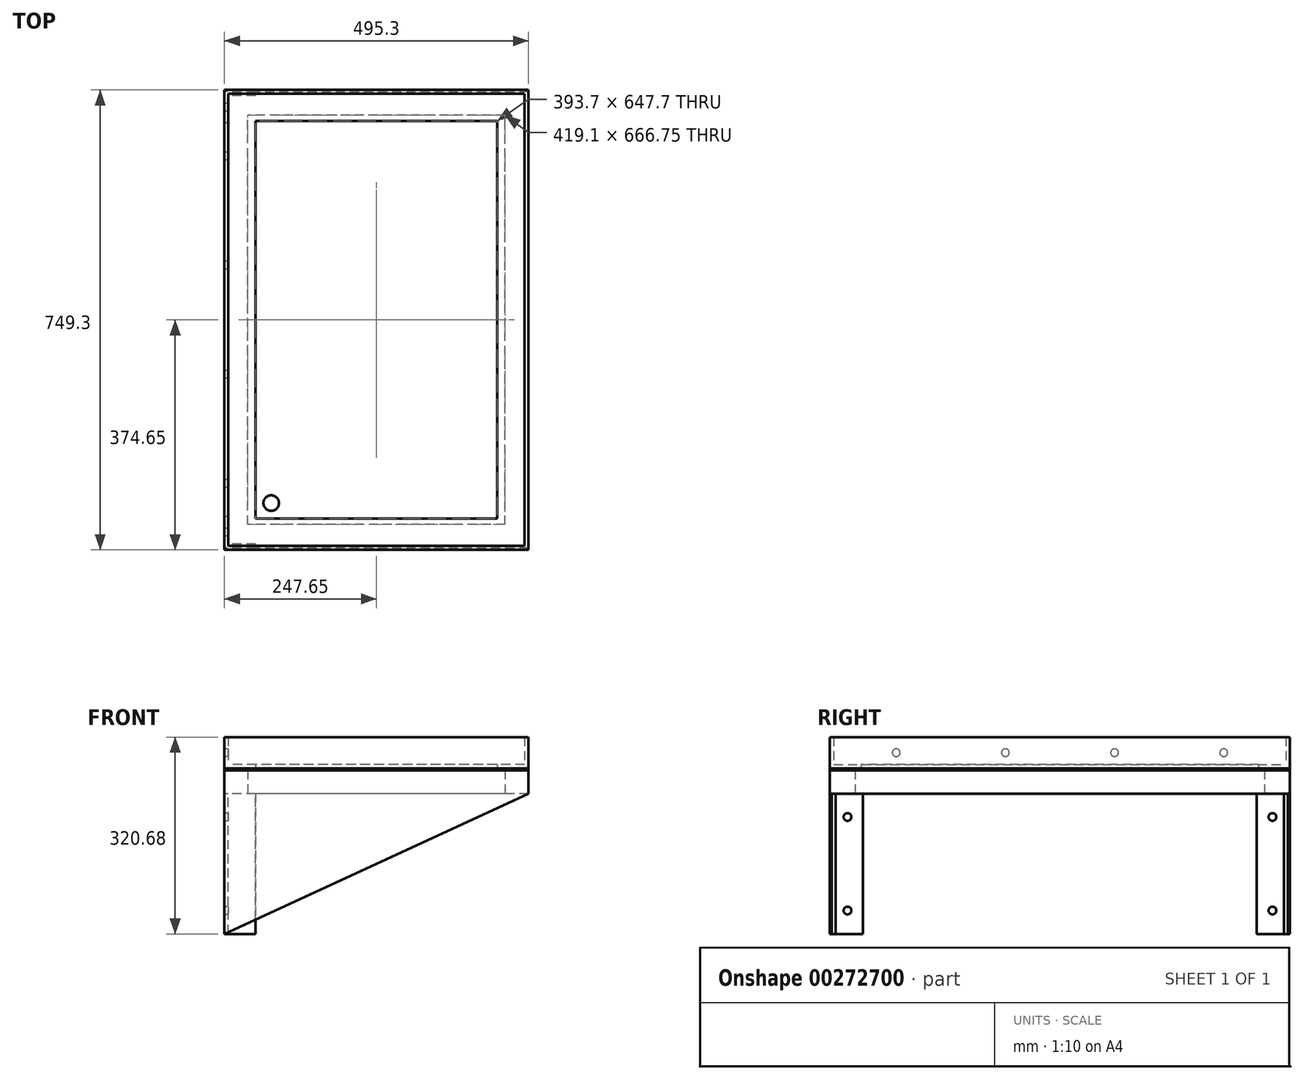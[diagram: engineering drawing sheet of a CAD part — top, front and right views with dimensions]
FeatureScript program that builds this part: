
annotation { "Feature Type Name" : "Feature", "Feature Type Description" : "" }
export const myFeature = defineFeature(function(context is Context, id is Id, definition is map)
    precondition{}
    {
        {
            var Q0;
            Q0=qCreatedBy(makeId("Top.planeOp"),FACE);
            var sketch = newSketch(context, id + "F0", { "sketchPlane" : qUnion([Q0])});
            skLineSegment(sketch, "E0.bottom", {"start": v(247.65, -371.47) * mm, "end": v(-247.65, -371.48) * mm});
            skLineSegment(sketch, "E0.top", {"start": v(247.65, 371.48) * mm, "end": v(-247.65, 371.48) * mm});
            skLineSegment(sketch, "E0.left", {"start": v(247.65, -371.47) * mm, "end": v(247.65, 371.48) * mm});
            skLineSegment(sketch, "E0.right", {"start": v(-247.65, -371.48) * mm, "end": v(-247.65, 371.48) * mm});
            skPoint(sketch, "E0.middle", {"position": v(0, 0) * mm});
            skLineSegment(sketch, "E1.0", {"start": v(-209.55, -333.38) * mm, "end": v(-209.55, 333.38) * mm});
            skLineSegment(sketch, "E1.1", {"start": v(209.55, -333.37) * mm, "end": v(-209.55, -333.38) * mm});
            skLineSegment(sketch, "E1.2", {"start": v(209.55, -333.37) * mm, "end": v(209.55, 333.38) * mm});
            skLineSegment(sketch, "E1.3", {"start": v(209.55, 333.38) * mm, "end": v(-209.55, 333.38) * mm});
            skSolve(sketch);
        }
        {
            var Q0;
            Q0 = qSketchRegion(id + "F0", true);
            extrude(context, id + "F1", {"entities" : qUnion([Q0]), "depth" : 38.1 * mm});
        }
        {
            var Q0;
            Q0=makeQuery(id+"F1.opExtrude","SWEPT_FACE",FACE,{"disambiguationData":[OSD([sQuery(id+"F0.wireOp",EDGE,"E0.bottom")])]});
            var sketch = newSketch(context, id + "F2", { "sketchPlane" : qUnion([Q0])});
            skLineSegment(sketch, "E2.0", {"start": v(247.65, 38.1) * mm, "end": v(-247.65, 38.1) * mm});
            skLineSegment(sketch, "E3", {"start": v(247.65, 0) * mm, "end": v(-247.65, -228.6) * mm});
            skLineSegment(sketch, "E4", {"start": v(-247.65, -228.6) * mm, "end": v(-247.65, 0) * mm});
            skLineSegment(sketch, "E5", {"start": v(-247.65, 0) * mm, "end": v(-247.65, 38.1) * mm});
            skLineSegment(sketch, "E6", {"start": v(247.65, 38.1) * mm, "end": v(247.65, 0) * mm});
            skSolve(sketch);
        }
        {
            var Q0;
            Q0=makeQuery(id+"F1.opExtrude","SWEPT_FACE",FACE,{"disambiguationData":[OSD([sQuery(id+"F0.wireOp",EDGE,"E0.top")])]});
            var sketch = newSketch(context, id + "F3", { "sketchPlane" : qUnion([Q0])});
            skLineSegment(sketch, "E7", {"start": v(-247.65, 0) * mm, "end": v(247.65, -228.6) * mm});
            skLineSegment(sketch, "E8", {"start": v(247.65, -228.6) * mm, "end": v(247.65, 0) * mm});
            skLineSegment(sketch, "E9", {"start": v(-247.65, 0) * mm, "end": v(-247.65, 38.1) * mm});
            skLineSegment(sketch, "E10", {"start": v(-247.65, 38.1) * mm, "end": v(247.65, 38.1) * mm});
            skLineSegment(sketch, "E11", {"start": v(247.65, 38.1) * mm, "end": v(247.65, 0) * mm});
            skSolve(sketch);
        }
        {
            var Q0;
            Q0 = qSketchRegion(id + "F2", true);
            extrude(context, id + "F4", {"entities" : qUnion([Q0]), "depth" : 3.17 * mm});
        }
        {
            var Q0;
            Q0 = qSketchRegion(id + "F3", true);
            extrude(context, id + "F5", {"entities" : qUnion([Q0]), "depth" : 3.17 * mm});
        }
        {
            var Q0;
            Q0=makeQuery(id+"F5.boolean.opBoolean","MERGE",FACE,{"derivedFrom":[makeQuery(id+"F4.boolean.opBoolean","MERGE",FACE,{"derivedFrom":[makeQuery(id+"F1.opExtrude","SWEPT_FACE",FACE,{"disambiguationData":[OSD([sQuery(id+"F0.wireOp",EDGE,"E0.right")])]}),makeQuery(id+"F4.opExtrude","SWEPT_FACE",FACE,{"disambiguationData":[OSD([sQuery(id+"F2.wireOp",EDGE,"E4")])]})]}),makeQuery(id+"F5.opExtrude","SWEPT_FACE",FACE,{"disambiguationData":[OSD([sQuery(id+"F3.wireOp",EDGE,"E8")])]})]});
            var sketch = newSketch(context, id + "F6", { "sketchPlane" : qUnion([Q0])});
            skLineSegment(sketch, "E12.0", {"start": v(371.47, 0) * mm, "end": v(-371.48, 0) * mm});
            skLineSegment(sketch, "E13", {"start": v(-320.68, -228.6) * mm, "end": v(-320.68, 0) * mm});
            skLineSegment(sketch, "E14", {"start": v(371.47, 0) * mm, "end": v(371.47, -228.6) * mm});
            skLineSegment(sketch, "E15", {"start": v(371.47, -228.6) * mm, "end": v(320.68, -228.6) * mm});
            skLineSegment(sketch, "E16", {"start": v(320.68, -228.6) * mm, "end": v(320.68, 0) * mm});
            skLineSegment(sketch, "E17", {"start": v(-320.68, -228.6) * mm, "end": v(-371.48, -228.6) * mm});
            skLineSegment(sketch, "E18", {"start": v(-371.48, 0) * mm, "end": v(-371.48, -228.6) * mm});
            skSolve(sketch);
        }
        {
            var Q0;
            Q0 = qSketchRegion(id + "F6", true);
            extrude(context, id + "F7", {"entities" : qUnion([Q0]), "oppositeDirection" : true, "depth" : 6.35 * mm});
        }
        {
            var Q0;
            Q0=makeQuery(id+"F7.opExtrude","CAP_FACE",FACE,{"disambiguationData":[OSD([sQuery(id+"F6.wireOp",EDGE,"E12.0"),sQuery(id+"F6.wireOp",EDGE,"e24fae86-0eb9-4a12-ab5b-77b361595a97.0"),sQuery(id+"F6.wireOp",EDGE,"e9ZgIQYv-HXcm-3d7P-bhbC-L1sBMD0jo2iH"),sQuery(id+"F6.wireOp",EDGE,"b7fAcNB5-LM3v-M6Ys-QrrH-VZOuPliIFRUq")])],"isStart":false});
            var sketch = newSketch(context, id + "F8", { "sketchPlane" : qUnion([Q0])});
            skLineSegment(sketch, "E19.bottom", {"start": v(-371.48, -228.6) * mm, "end": v(-365.13, -228.6) * mm});
            skLineSegment(sketch, "E19.top", {"start": v(-371.48, 0) * mm, "end": v(-365.13, 0) * mm});
            skLineSegment(sketch, "E19.left", {"start": v(-371.48, -228.6) * mm, "end": v(-371.48, 0) * mm});
            skLineSegment(sketch, "E19.right", {"start": v(-365.13, -228.6) * mm, "end": v(-365.13, 0) * mm});
            skSolve(sketch);
        }
        {
            var Q0;
            Q0 = qSketchRegion(id + "F8", true);
            extrude(context, id + "F9", {"entities" : qUnion([Q0]), "operationType" : NewBodyOperationType.ADD, "depth" : 44.45 * mm});
        }
        {
            var Q0;
            Q0=makeQuery(id+"F7.opExtrude","CAP_FACE",FACE,{"disambiguationData":[OSD([sQuery(id+"F6.wireOp",EDGE,"f5ba7e4f-57d3-4fa4-9deb-a295e54d8ec9.0"),sQuery(id+"F6.wireOp",EDGE,"E12.0"),sQuery(id+"F6.wireOp",EDGE,"EwE4f2qn-rMHZ-ifyL-MpHM-OiWTRZvf5JZf"),sQuery(id+"F6.wireOp",EDGE,"E13")])],"isStart":false});
            var sketch = newSketch(context, id + "F10", { "sketchPlane" : qUnion([Q0])});
            skLineSegment(sketch, "E20.bottom", {"start": v(371.48, -228.6) * mm, "end": v(365.13, -228.6) * mm});
            skLineSegment(sketch, "E20.top", {"start": v(371.48, 0) * mm, "end": v(365.13, 0) * mm});
            skLineSegment(sketch, "E20.left", {"start": v(371.48, -228.6) * mm, "end": v(371.48, 0) * mm});
            skLineSegment(sketch, "E20.right", {"start": v(365.13, -228.6) * mm, "end": v(365.13, 0) * mm});
            skSolve(sketch);
        }
        {
            var Q0;
            Q0 = qSketchRegion(id + "F10", true);
            extrude(context, id + "F11", {"entities" : qUnion([Q0]), "operationType" : NewBodyOperationType.ADD, "depth" : 44.45 * mm});
        }
        {
            var Q0;
            Q0=makeQuery(id+"F1.opExtrude","CAP_FACE",FACE,{"disambiguationData":[OSD([sQuery(id+"F0.wireOp",EDGE,"E0.bottom"),sQuery(id+"F0.wireOp",EDGE,"E0.top"),sQuery(id+"F0.wireOp",EDGE,"E0.left"),sQuery(id+"F0.wireOp",EDGE,"E0.right"),sQuery(id+"F0.wireOp",EDGE,"E1.0"),sQuery(id+"F0.wireOp",EDGE,"E1.1"),sQuery(id+"F0.wireOp",EDGE,"E1.2"),sQuery(id+"F0.wireOp",EDGE,"E1.3")])],"isStart":false});
            var sketch = newSketch(context, id + "F12", { "sketchPlane" : qUnion([Q0])});
            skLineSegment(sketch, "E21.0", {"start": v(247.65, 374.65) * mm, "end": v(-247.65, 374.65) * mm});
            skLineSegment(sketch, "E22.0", {"start": v(247.65, -374.65) * mm, "end": v(-247.65, -374.65) * mm});
            skLineSegment(sketch, "E23", {"start": v(-247.65, -374.65) * mm, "end": v(-247.65, 374.65) * mm});
            skLineSegment(sketch, "E24", {"start": v(247.65, 374.65) * mm, "end": v(247.65, -374.65) * mm});
            skCircle(sketch, "E25", {"center": v(-171.45, -298.45) * mm, "radius": 12.7 * mm});
            skSolve(sketch);
        }
        {
            var Q0;
            Q0 = qSketchRegion(id + "F12", true);
            extrude(context, id + "F13", {"entities" : qUnion([Q0]), "depth" : 3.17 * mm});
        }
        {
            var Q0;
            Q0=makeQuery(id+"F13.opExtrude","CAP_FACE",FACE,{"disambiguationData":[OSD([sQuery(id+"F12.wireOp",EDGE,"E21.0"),sQuery(id+"F12.wireOp",EDGE,"E22.0"),sQuery(id+"F12.wireOp",EDGE,"E23"),sQuery(id+"F12.wireOp",EDGE,"E24")])],"isStart":false});
            var sketch = newSketch(context, id + "F14", { "sketchPlane" : qUnion([Q0])});
            skLineSegment(sketch, "E26.0.0", {"start": v(247.65, -374.65) * mm, "end": v(247.65, 374.65) * mm});
            skLineSegment(sketch, "E26.0.1", {"start": v(247.65, 374.65) * mm, "end": v(-247.65, 374.65) * mm});
            skLineSegment(sketch, "E26.0.2", {"start": v(-247.65, 374.65) * mm, "end": v(-247.65, -374.65) * mm});
            skLineSegment(sketch, "E26.0.3", {"start": v(-247.65, -374.65) * mm, "end": v(247.65, -374.65) * mm});
            skLineSegment(sketch, "E27.0", {"start": v(-196.85, 323.85) * mm, "end": v(-196.85, -323.85) * mm});
            skLineSegment(sketch, "E27.1", {"start": v(196.85, 323.85) * mm, "end": v(-196.85, 323.85) * mm});
            skLineSegment(sketch, "E27.2", {"start": v(196.85, -323.85) * mm, "end": v(196.85, 323.85) * mm});
            skLineSegment(sketch, "E27.3", {"start": v(-196.85, -323.85) * mm, "end": v(196.85, -323.85) * mm});
            skSolve(sketch);
        }
        {
            var Q0;
            Q0 = qSketchRegion(id + "F14", true);
            extrude(context, id + "F15", {"entities" : qUnion([Q0]), "depth" : 6.35 * mm});
        }
        {
            var Q0;
            Q0=makeQuery(id+"F15.opExtrude","CAP_FACE",FACE,{"disambiguationData":[OSD([sQuery(id+"F14.wireOp",EDGE,"E26.0.0"),sQuery(id+"F14.wireOp",EDGE,"E26.0.1"),sQuery(id+"F14.wireOp",EDGE,"E26.0.2"),sQuery(id+"F14.wireOp",EDGE,"E26.0.3"),sQuery(id+"F14.wireOp",EDGE,"E27.0"),sQuery(id+"F14.wireOp",EDGE,"E27.1"),sQuery(id+"F14.wireOp",EDGE,"E27.2"),sQuery(id+"F14.wireOp",EDGE,"E27.3")])],"isStart":false});
            var sketch = newSketch(context, id + "F16", { "sketchPlane" : qUnion([Q0])});
            skLineSegment(sketch, "E28.0.0", {"start": v(247.65, -374.65) * mm, "end": v(247.65, 374.65) * mm});
            skLineSegment(sketch, "E28.0.1", {"start": v(247.65, 374.65) * mm, "end": v(-247.65, 374.65) * mm});
            skLineSegment(sketch, "E28.0.2", {"start": v(-247.65, 374.65) * mm, "end": v(-247.65, -374.65) * mm});
            skLineSegment(sketch, "E28.0.3", {"start": v(-247.65, -374.65) * mm, "end": v(247.65, -374.65) * mm});
            skLineSegment(sketch, "E29.0", {"start": v(241.3, 368.3) * mm, "end": v(-241.3, 368.3) * mm});
            skLineSegment(sketch, "E29.1", {"start": v(241.3, -368.3) * mm, "end": v(241.3, 368.3) * mm});
            skLineSegment(sketch, "E29.2", {"start": v(-241.3, -368.3) * mm, "end": v(241.3, -368.3) * mm});
            skLineSegment(sketch, "E29.3", {"start": v(-241.3, 368.3) * mm, "end": v(-241.3, -368.3) * mm});
            skSolve(sketch);
        }
        {
            var Q0;
            Q0 = qSketchRegion(id + "F16", true);
            extrude(context, id + "F17", {"entities" : qUnion([Q0]), "operationType" : NewBodyOperationType.ADD, "depth" : 44.45 * mm});
        }
        {
            var Q0;
            Q0=makeQuery(id+"F17.boolean.opBoolean","MERGE",FACE,{"derivedFrom":[makeQuery(id+"F15.opExtrude","SWEPT_FACE",FACE,{"disambiguationData":[OSD([sQuery(id+"F14.wireOp",EDGE,"E26.0.2")])]}),makeQuery(id+"F17.opExtrude","SWEPT_FACE",FACE,{"disambiguationData":[OSD([sQuery(id+"F16.wireOp",EDGE,"E28.0.2")])]})]});
            var sketch = newSketch(context, id + "F18", { "sketchPlane" : qUnion([Q0])});
            skCircle(sketch, "E30", {"center": v(-266.7, 66.67) * mm, "radius": 6.35 * mm});
            skCircle(sketch, "E31", {"center": v(-88.9, 66.67) * mm, "radius": 6.35 * mm});
            skCircle(sketch, "E32", {"center": v(88.9, 66.67) * mm, "radius": 6.35 * mm});
            skCircle(sketch, "E33", {"center": v(266.7, 66.67) * mm, "radius": 6.35 * mm});
            skCircle(sketch, "E34", {"center": v(-346.08, -38.1) * mm, "radius": 6.35 * mm});
            skCircle(sketch, "E35", {"center": v(-346.08, -190.5) * mm, "radius": 6.35 * mm});
            skCircle(sketch, "E36", {"center": v(346.07, -38.1) * mm, "radius": 6.35 * mm});
            skCircle(sketch, "E37", {"center": v(346.07, -190.5) * mm, "radius": 6.35 * mm});
            skSolve(sketch);
        }
        {
            var Q0;
            Q0 = qSketchRegion(id + "F18", true);
            extrude(context, id + "F19", {"entities" : qUnion([Q0]), "operationType" : NewBodyOperationType.REMOVE, "oppositeDirection" : true, "depth" : 25.4 * mm});
        }
    });
